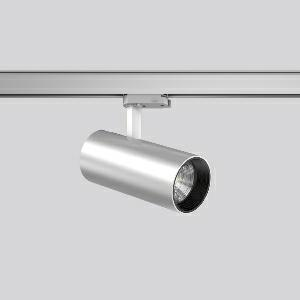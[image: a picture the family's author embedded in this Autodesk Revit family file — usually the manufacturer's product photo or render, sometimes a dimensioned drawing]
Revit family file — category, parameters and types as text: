
# Revit family: deecos_s_mini_742198_004_1_56cf
name_source: partatom
category: Lighting Fixtures
units: mm (PartAtom-declared; Revit-internal decimal feet)

## family parameters
Cut with Voids When Loaded = No
Host = Face
Light Source = No
Part Type = Normal
Room Calculation Point = No
Round Connector Dimension = Use Diameter
Shared = No

## types (1)
- DEECOS S mini (1 x LED Modul 940, 2400 lm, 4000)
    Apparent Load = 20 VA
    Approval mark = CE
    CIE Flux Codes = 99 100 100 100 100
    Color Rendering = 92
    Color Temperature = 4000
    Default Elevation = 1800 mm
    Description = Series: DEECOS S mini
LED surface-mounted projector in modern design with no visible cooling ribs. Housing: die-cast aluminium, powder-coated. Rotation range: 356°. Swivel range: 90°. Black plastic ring and recessed LED to prevent glare from the side. Optical assembly with lens made of plastic (polycarbonate) for the best homogeneous light distribution - can be changed without tools. Best colour rendering index Ra>90. With multi adaptor for 3-circuit tracks 230 V. Suitable for Track on ceiling, Wall track. High quality converter without flickering and stroboscopic effect. The following accessories can be mounted without use of tools: interchangeable lenses, decorative glasses, honeycomb louvre, clear and frosted diffusers, white interchangeable plastic ring. 
Colour: silver
Diameter: 87 mm
Height: 214 mm
Lamp: LED
Socket: without socket
Colour temperature: 4000K
Colour rendering index (CRI): 92
System power: 20 W
Rated luminous flux: 2400 lm
Luminous efficiency: 120 lm/W
Control gear: Regulated power supply
Protection class: I
Type of protection: IP 20
    Height = 214 mm
    Lamp = 1 x LED Modul 940
    Lamp Light Flux = 2400 lm
    Lamp count = 1
    Length = 87 mm
    Lifetime = 50000 h
    Luminous efficacy = 120 lm/W
    Manufacturer = RZB
    ModVariant = No
    Model = 742198.004.1
    Mounting Place = Ceiling
    Mounting Type = Rail mounted
    Number of Poles = 1
    OnlyDefault = Yes
    Power Factor = 1
    Product Name = DEECOS S mini
    Product group = Track mounted projectors
    ProductGroupID = 301
    Protection Class = Protection class I
    Protection Degree = IP 20
    RLX_Detail_Level = 1
    RLX_Emergency_Light_Flux = 0 lm
    RLX_Emergency_Type = 0
    RLX_Emergency_Type_DB = No
    RlxData = <blob elided: 37557 chars, md5=e13e747a>
    Socket = socket
    Standby Power = 0 W
    System Light Flux = 2400 lm
    System Power = 20 W
    Type Comments = Product without accessories
    Type Image = 741930.004.jpg
    URL = http://relux.com
    VarID = ---
    Voltage = 230 V
    Voltage Range = 220-240 V
    Weight = 0.00 kg
    Width = 0 mm  [stored 0 ft]

note: [stored X ft] marks values corroborated as IEEE doubles in the binary element streams (Revit-internal decimal feet)

## geometry (parser evidence)
native form markers: Blend x4, Sweep x14
no freeform markers — native parametric forms only
